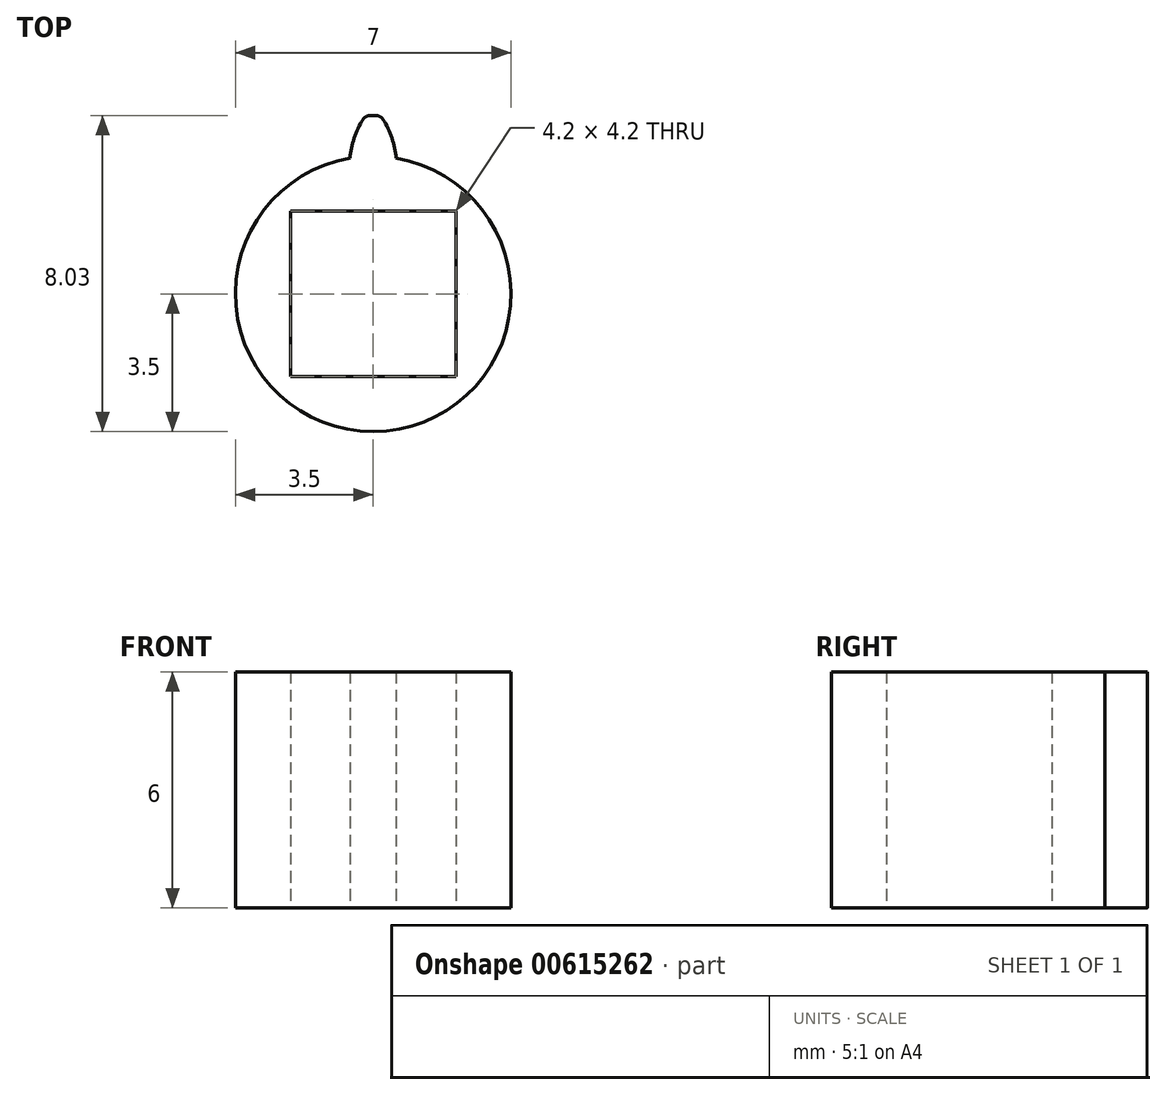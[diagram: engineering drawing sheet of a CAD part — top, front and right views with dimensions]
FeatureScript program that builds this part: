
annotation { "Feature Type Name" : "Feature", "Feature Type Description" : "" }
export const myFeature = defineFeature(function(context is Context, id is Id, definition is map)
    precondition{}
    {
        {
            var Q0;
            Q0=qCreatedBy(makeId("Top.planeOp"),FACE);
            var sketch = newSketch(context, id + "F0", { "sketchPlane" : qUnion([Q0])});
            skCircle(sketch, "E0", {"center": v(0, 0) * mm, "radius": 3.5 * mm});
            skLineSegment(sketch, "E1", {"start": v(0, 3.5) * mm, "end": v(0, -3.5) * mm, "construction": true});
            skLineSegment(sketch, "E2", {"start": v(-0.46, 3.47) * mm, "end": v(0, 0) * mm, "construction": true});
            skLineSegment(sketch, "E3", {"start": v(-1.34, 3.23) * mm, "end": v(0, 0) * mm, "construction": true});
            skLineSegment(sketch, "E4", {"start": v(-2.13, 2.78) * mm, "end": v(0, 0) * mm, "construction": true});
            skLineSegment(sketch, "E5", {"start": v(0.46, 3.47) * mm, "end": v(0, 0) * mm, "construction": true});
            skLineSegment(sketch, "E6", {"start": v(0, 0) * mm, "end": v(1.17, 3.3) * mm, "construction": true});
            skLineSegment(sketch, "E7", {"start": v(1.98, 2.88) * mm, "end": v(0, 0) * mm, "construction": true});
            skLineSegment(sketch, "E8", {"start": v(0, 0) * mm, "end": v(-2.78, 2.13) * mm, "construction": true});
            skLineSegment(sketch, "E9", {"start": v(0, 0) * mm, "end": v(2.66, 2.27) * mm, "construction": true});
            skLineSegment(sketch, "E10.bottom", {"start": v(2.1, -2.1) * mm, "end": v(-2.1, -2.1) * mm});
            skLineSegment(sketch, "E10.top", {"start": v(2.1, 2.1) * mm, "end": v(-2.1, 2.1) * mm});
            skLineSegment(sketch, "E10.left", {"start": v(2.1, -2.1) * mm, "end": v(2.1, 2.1) * mm});
            skLineSegment(sketch, "E10.right", {"start": v(-2.1, -2.1) * mm, "end": v(-2.1, 2.1) * mm});
            skLineSegment(sketch, "E11", {"start": v(-0.46, 3.47) * mm, "end": v(0.7, 3.62) * mm, "construction": true});
            skLineSegment(sketch, "E12", {"start": v(-1.34, 3.23) * mm, "end": v(0.83, 4.13) * mm, "construction": true});
            skLineSegment(sketch, "E13", {"start": v(-2.13, 2.78) * mm, "end": v(0.67, 4.92) * mm, "construction": true});
            skLineSegment(sketch, "E14", {"start": v(-2.78, 2.13) * mm, "end": v(0.03, 5.8) * mm, "construction": true});
            skArc(sketch, "E15", {"start": v(0.58, 3.45) * mm, "mid": v(0.41, 4.12) * mm, "end": v(0.05, 4.7) * mm});
            skArc(sketch, "E16.MirrorCS", {"start": v(-0.6, 3.45) * mm, "mid": v(-0.42, 4.12) * mm, "end": v(-0.06, 4.7) * mm});
            skLineSegment(sketch, "E17", {"start": v(-0.2, 4.53) * mm, "end": v(0.19, 4.53) * mm});
            skSolve(sketch);
        }
        {
            var Q0;
            {var subQ0=sQuery(id+"F0.wireOp",EDGE,"E0");var subQ1=makeQuery(id+"F0.imprint","INTERSECT",VERTEX,{"derivedFrom":[subQ0,sQuery(id+"F0.wireOp",EDGE,"QxTWC7Lz-du55-Eq41-CNKB-dq2QVF1DEtN8")]});Q0=makeQuery(id+"F0.imprint","IMPRINT",FACE,{"disambiguationData":[TD([[makeQuery(id+"F0.imprint","IMPRINT",EDGE,{"disambiguationData":[TD([[subQ1,-1.0]])],"derivedFrom":subQ0}),1.0]])]});}
            extrude(context, id + "F1", {"entities" : qUnion([Q0]), "depth" : 6 * mm, "offsetDistance" : 25 * mm});
        }
        {
            var Q0;
            {var subQ5=sQuery(id+"F0.wireOp",EDGE,"E17");Q0=makeQuery(id+"F0.imprint","IMPRINT",FACE,{"disambiguationData":[TD([[makeQuery(id+"F0.imprint","IMPRINT",EDGE,{"derivedFrom":subQ5}),-1.0]])]});}
            extrude(context, id + "F2", {"entities" : qUnion([Q0]), "operationType" : NewBodyOperationType.ADD, "depth" : 6 * mm, "offsetDistance" : 25 * mm});
        }
        {
            var Q0;
            Q0=makeQuery(id+"F2.opExtrude","SWEPT_EDGE",EDGE,{"disambiguationData":[OSD([sQuery(id+"F0.wireOp",EDGE,"8ff6aac1-0804-49f7-ba98-cac151a97ee40.MirrorCS"),sQuery(id+"F0.wireOp",EDGE,"jLX3nK70-xnrL-4WXP-K6oy-EgnrdlAAAHqw")])]});
            var Q1;
            Q1=makeQuery(id+"F2.opExtrude","SWEPT_EDGE",EDGE,{"disambiguationData":[OSD([sQuery(id+"F0.wireOp",EDGE,"E0"),sQuery(id+"F0.wireOp",EDGE,"8ff6aac1-0804-49f7-ba98-cac151a97ee40.MirrorCS")])]});
            var Q2;
            Q2=makeQuery(id+"F2.opExtrude","SWEPT_EDGE",EDGE,{"disambiguationData":[OSD([sQuery(id+"F0.wireOp",EDGE,"jmpbCdDG-YTDs-J9VS-SbC6-E6aQ3DWbFFUO"),sQuery(id+"F0.wireOp",EDGE,"jLX3nK70-xnrL-4WXP-K6oy-EgnrdlAAAHqw")])]});
            var Q3;
            Q3=makeQuery(id+"F2.opExtrude","SWEPT_EDGE",EDGE,{"disambiguationData":[OSD([sQuery(id+"F0.wireOp",EDGE,"E0"),sQuery(id+"F0.wireOp",EDGE,"jmpbCdDG-YTDs-J9VS-SbC6-E6aQ3DWbFFUO")])]});
            var Q4;
            Q4=makeQuery(id+"F2.opExtrude","SWEPT_EDGE",EDGE,{"disambiguationData":[OSD([sQuery(id+"F0.wireOp",EDGE,"E16.MirrorCS"),sQuery(id+"F0.wireOp",EDGE,"E17")])]});
            var Q5;
            Q5=makeQuery(id+"F2.opExtrude","SWEPT_EDGE",EDGE,{"disambiguationData":[OSD([sQuery(id+"F0.wireOp",EDGE,"E15"),sQuery(id+"F0.wireOp",EDGE,"E17")])]});
            fillet(context, id + "F3", {"entities" : qUnion([Q0, Q1, Q2, Q3, Q4, Q5]), "radius" : .2 * mm, "tangentPropagation" : true, "allowEdgeOverflow" : false});
        }
    });
